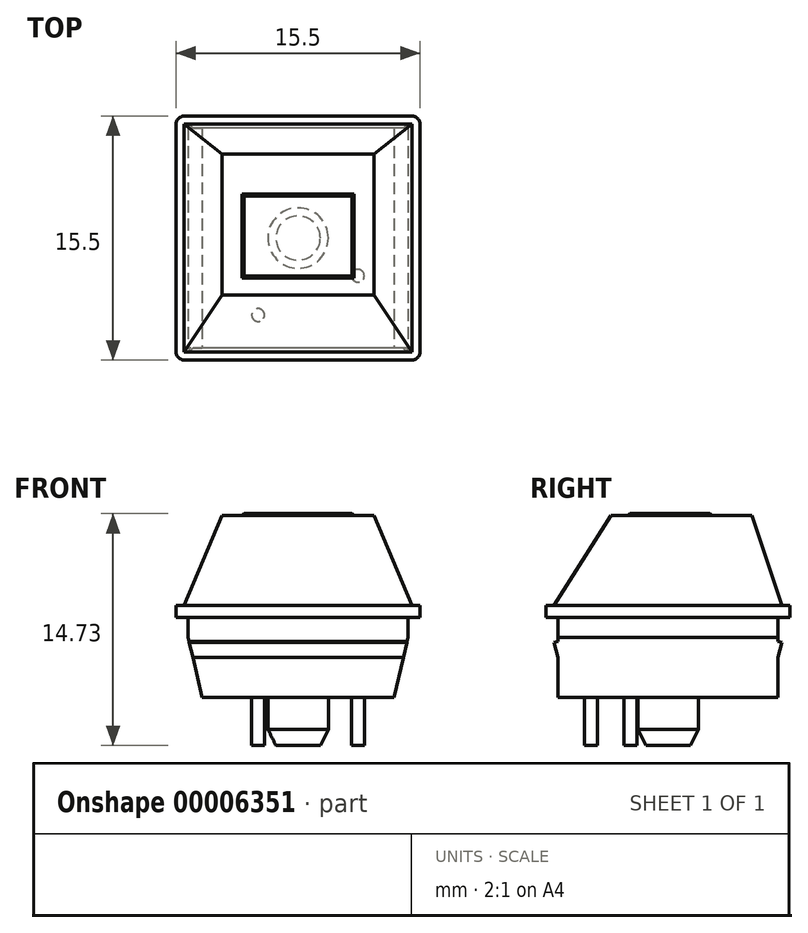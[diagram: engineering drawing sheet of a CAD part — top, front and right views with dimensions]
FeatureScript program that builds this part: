
annotation { "Feature Type Name" : "Feature", "Feature Type Description" : "" }
export const myFeature = defineFeature(function(context is Context, id is Id, definition is map)
    precondition{}
    {
        {
            var Q0;
            Q0=qCreatedBy(makeId("Top.planeOp"),FACE);
            var sketch = newSketch(context, id + "F0", { "sketchPlane" : qUnion([Q0])});
            skLineSegment(sketch, "E0.bottom", {"start": v(-7.24, 7.75) * mm, "end": v(7.24, 7.75) * mm});
            skLineSegment(sketch, "E0.top", {"start": v(-7.24, -7.75) * mm, "end": v(7.24, -7.75) * mm});
            skLineSegment(sketch, "E0.left", {"start": v(-7.75, 7.24) * mm, "end": v(-7.75, -7.24) * mm});
            skLineSegment(sketch, "E0.right", {"start": v(7.75, 7.24) * mm, "end": v(7.75, -7.24) * mm});
            skPoint(sketch, "E1", {"position": v(0, 7.75) * mm});
            skPoint(sketch, "E2", {"position": v(-7.75, 0) * mm});
            skPoint(sketch, "E3.visualSharp", {"position": v(-7.75, 7.75) * mm});
            skArc(sketch, "E3.filletArc", {"start": v(-7.24, 7.75) * mm, "mid": v(-7.6, 7.6) * mm, "end": v(-7.75, 7.24) * mm});
            skPoint(sketch, "E4.visualSharp", {"position": v(7.75, 7.75) * mm});
            skArc(sketch, "E4.filletArc", {"start": v(7.75, 7.24) * mm, "mid": v(7.6, 7.6) * mm, "end": v(7.24, 7.75) * mm});
            skPoint(sketch, "E5.visualSharp", {"position": v(7.75, -7.75) * mm});
            skArc(sketch, "E5.filletArc", {"start": v(7.24, -7.75) * mm, "mid": v(7.6, -7.6) * mm, "end": v(7.75, -7.24) * mm});
            skPoint(sketch, "E6.visualSharp", {"position": v(-7.75, -7.75) * mm});
            skArc(sketch, "E6.filletArc", {"start": v(-7.75, -7.24) * mm, "mid": v(-7.6, -7.6) * mm, "end": v(-7.24, -7.75) * mm});
            skSolve(sketch);
        }
        {
            var Q0;
            Q0 = qSketchRegion(id + "F0", true);
            extrude(context, id + "F1", {"entities" : qUnion([Q0]), "depth" : 11.68 * mm});
        }
        {
            var Q0;
            Q0=makeQuery(id+"F1.opExtrude","SWEPT_FACE",FACE,{"disambiguationData":[OSD([sQuery(id+"F0.wireOp",EDGE,"E0.top")])]});
            var sketch = newSketch(context, id + "F2", { "sketchPlane" : qUnion([Q0])});
            skLineSegment(sketch, "E7", {"start": v(-3.43, 11.68) * mm, "end": v(-3.56, 11.56) * mm});
            skLineSegment(sketch, "E8", {"start": v(-3.56, 11.56) * mm, "end": v(-4.83, 11.56) * mm});
            skLineSegment(sketch, "E9", {"start": v(-4.83, 11.56) * mm, "end": v(-7.24, 5.84) * mm});
            skLineSegment(sketch, "E10", {"start": v(-7.24, 5.84) * mm, "end": v(-7.75, 5.84) * mm});
            skLineSegment(sketch, "E11", {"start": v(-7.75, 5.84) * mm, "end": v(-7.75, 11.68) * mm});
            skLineSegment(sketch, "E12", {"start": v(-7.75, 11.68) * mm, "end": v(-3.43, 11.68) * mm});
            skLineSegment(sketch, "E13", {"start": v(-7.75, 5.08) * mm, "end": v(-6.99, 5.08) * mm});
            skLineSegment(sketch, "E14", {"start": v(-6.98, 5.08) * mm, "end": v(-6.98, 3.81) * mm});
            skLineSegment(sketch, "E15", {"start": v(-6.99, 3.81) * mm, "end": v(-6.1, 0) * mm});
            skLineSegment(sketch, "E16", {"start": v(-6.1, 0) * mm, "end": v(-7.75, 0) * mm});
            skLineSegment(sketch, "E17", {"start": v(-7.75, 0) * mm, "end": v(-7.75, 5.08) * mm});
            skLineSegment(sketch, "E18", {"start": v(0, 11.68) * mm, "end": v(0, 0) * mm, "construction": true});
            skLineSegment(sketch, "E19.0.MirrorCS", {"start": v(3.43, 11.68) * mm, "end": v(3.56, 11.56) * mm});
            skLineSegment(sketch, "E19.1.MirrorCS", {"start": v(6.99, 5.08) * mm, "end": v(6.99, 3.81) * mm});
            skLineSegment(sketch, "E19.2.MirrorCS", {"start": v(3.56, 11.56) * mm, "end": v(4.83, 11.56) * mm});
            skLineSegment(sketch, "E19.3.MirrorCS", {"start": v(6.99, 3.81) * mm, "end": v(6.1, 0) * mm});
            skLineSegment(sketch, "E19.4.MirrorCS", {"start": v(4.83, 11.56) * mm, "end": v(7.24, 5.84) * mm});
            skLineSegment(sketch, "E19.5.MirrorCS", {"start": v(6.1, 0) * mm, "end": v(7.75, 0) * mm});
            skLineSegment(sketch, "E19.6.MirrorCS", {"start": v(7.24, 5.84) * mm, "end": v(7.75, 5.84) * mm});
            skLineSegment(sketch, "E19.7.MirrorCS", {"start": v(7.75, 0) * mm, "end": v(7.75, 5.08) * mm});
            skLineSegment(sketch, "E19.8.MirrorCS", {"start": v(7.75, 5.08) * mm, "end": v(6.99, 5.08) * mm});
            skLineSegment(sketch, "E19.9.MirrorCS", {"start": v(7.75, 5.84) * mm, "end": v(7.75, 11.68) * mm});
            skLineSegment(sketch, "E19.10.MirrorCS", {"start": v(7.75, 11.68) * mm, "end": v(3.43, 11.68) * mm});
            skSolve(sketch);
        }
        {
            var Q0;
            Q0 = qSketchRegion(id + "F2", true);
            extrude(context, id + "F3", {"entities" : qUnion([Q0]), "operationType" : NewBodyOperationType.REMOVE, "endBound" : BoundingType.THROUGH_ALL, "oppositeDirection" : true, "depth" : 25.4 * mm});
        }
        {
            var Q0;
            Q0=makeQuery(id+"F1.opExtrude","SWEPT_FACE",FACE,{"disambiguationData":[OSD([sQuery(id+"F0.wireOp",EDGE,"E0.left")])]});
            var sketch = newSketch(context, id + "F4", { "sketchPlane" : qUnion([Q0])});
            skLineSegment(sketch, "E20", {"start": v(-7.75, 5.08) * mm, "end": v(-6.99, 5.08) * mm});
            skLineSegment(sketch, "E21", {"start": v(-6.99, 5.08) * mm, "end": v(-6.99, 3.56) * mm});
            skLineSegment(sketch, "E22", {"start": v(-6.99, 2.54) * mm, "end": v(-6.99, 0) * mm});
            skLineSegment(sketch, "E23", {"start": v(-6.99, 0) * mm, "end": v(-7.75, 0) * mm});
            skLineSegment(sketch, "E24", {"start": v(-7.75, 0) * mm, "end": v(-7.75, 5.08) * mm});
            skPoint(sketch, "E25", {"position": v(-6.99, 2.54) * mm});
            skLineSegment(sketch, "E26", {"start": v(-6.99, 3.56) * mm, "end": v(-7.24, 3.49) * mm});
            skLineSegment(sketch, "E27", {"start": v(-7.24, 3.49) * mm, "end": v(-6.99, 2.54) * mm});
            skLineSegment(sketch, "E28", {"start": v(0, 0) * mm, "end": v(0, 2.67) * mm, "construction": true});
            skLineSegment(sketch, "E29.0.MirrorCS", {"start": v(6.99, 3.56) * mm, "end": v(7.24, 3.49) * mm});
            skLineSegment(sketch, "E29.1.MirrorCS", {"start": v(7.75, 5.08) * mm, "end": v(6.99, 5.08) * mm});
            skLineSegment(sketch, "E29.2.MirrorCS", {"start": v(6.99, 0) * mm, "end": v(7.75, 0) * mm});
            skPoint(sketch, "E29.3.MirrorP", {"position": v(6.99, 2.54) * mm});
            skLineSegment(sketch, "E29.4.MirrorCS", {"start": v(7.75, 0) * mm, "end": v(7.75, 5.08) * mm});
            skLineSegment(sketch, "E29.5.MirrorCS", {"start": v(6.99, 2.54) * mm, "end": v(6.99, 0) * mm});
            skLineSegment(sketch, "E29.6.MirrorCS", {"start": v(6.99, 5.08) * mm, "end": v(6.99, 3.56) * mm});
            skLineSegment(sketch, "E29.7.MirrorCS", {"start": v(7.24, 3.49) * mm, "end": v(6.99, 2.54) * mm});
            skLineSegment(sketch, "E30", {"start": v(-7.75, 5.84) * mm, "end": v(-7.24, 5.84) * mm});
            skLineSegment(sketch, "E31", {"start": v(-7.24, 5.84) * mm, "end": v(-5.33, 11.56) * mm});
            skLineSegment(sketch, "E32", {"start": v(-5.33, 11.56) * mm, "end": v(-2.8, 11.56) * mm});
            skLineSegment(sketch, "E33", {"start": v(-2.8, 11.56) * mm, "end": v(-2.67, 11.68) * mm});
            skLineSegment(sketch, "E34", {"start": v(-2.67, 11.68) * mm, "end": v(-7.75, 11.68) * mm});
            skLineSegment(sketch, "E35", {"start": v(-7.75, 11.68) * mm, "end": v(-7.75, 5.84) * mm});
            skLineSegment(sketch, "E36", {"start": v(7.75, 5.84) * mm, "end": v(7.24, 5.84) * mm});
            skLineSegment(sketch, "E37", {"start": v(7.24, 5.84) * mm, "end": v(3.63, 11.56) * mm});
            skLineSegment(sketch, "E38", {"start": v(3.63, 11.56) * mm, "end": v(2.54, 11.56) * mm});
            skLineSegment(sketch, "E39", {"start": v(2.54, 11.56) * mm, "end": v(2.41, 11.68) * mm});
            skLineSegment(sketch, "E40", {"start": v(2.41, 11.68) * mm, "end": v(7.75, 11.68) * mm});
            skLineSegment(sketch, "E41", {"start": v(7.75, 11.68) * mm, "end": v(7.75, 5.84) * mm});
            skSolve(sketch);
        }
        {
            var Q0;
            Q0 = qSketchRegion(id + "F4", true);
            extrude(context, id + "F5", {"entities" : qUnion([Q0]), "operationType" : NewBodyOperationType.REMOVE, "endBound" : BoundingType.THROUGH_ALL, "oppositeDirection" : true, "depth" : 25.4 * mm});
        }
        {
            var Q0;
            Q0=makeQuery(id+"F1.opExtrude","CAP_FACE",FACE,{"disambiguationData":[OSD([sQuery(id+"F0.wireOp",EDGE,"E0.bottom"),sQuery(id+"F0.wireOp",EDGE,"E0.top"),sQuery(id+"F0.wireOp",EDGE,"E0.left"),sQuery(id+"F0.wireOp",EDGE,"E0.right"),sQuery(id+"F0.wireOp",EDGE,"E3.filletArc"),sQuery(id+"F0.wireOp",EDGE,"E4.filletArc"),sQuery(id+"F0.wireOp",EDGE,"E5.filletArc"),sQuery(id+"F0.wireOp",EDGE,"E6.filletArc")])],"isStart":true});
            var sketch = newSketch(context, id + "F6", { "sketchPlane" : qUnion([Q0])});
            skCircle(sketch, "E42", {"center": v(0, 0) * mm, "radius": 1.92 * mm});
            skCircle(sketch, "E43", {"center": v(3.8, 2.4) * mm, "radius": 0.4 * mm});
            skCircle(sketch, "E44", {"center": v(-2.54, 4.89) * mm, "radius": 0.4 * mm});
            skSolve(sketch);
        }
        {
            var Q0;
            Q0 = qSketchRegion(id + "F6", true);
            extrude(context, id + "F7", {"entities" : qUnion([Q0]), "operationType" : NewBodyOperationType.ADD, "depth" : 3.05 * mm});
        }
        {
            var Q0;
            Q0=makeQuery(id+"F7.opExtrude","CAP_FACE",FACE,{"disambiguationData":[OSD([sQuery(id+"F6.wireOp",EDGE,"E42")])],"isStart":false});
            chamfer(context, id + "F8", {"entities" : qUnion([Q0]), "chamferType" : ChamferType.TWO_OFFSETS, "width1" : 0.5 * mm, "oppositeDirection" : false, "width2" : 1.02 * mm, "tangentPropagation" : true});
        }
    });
